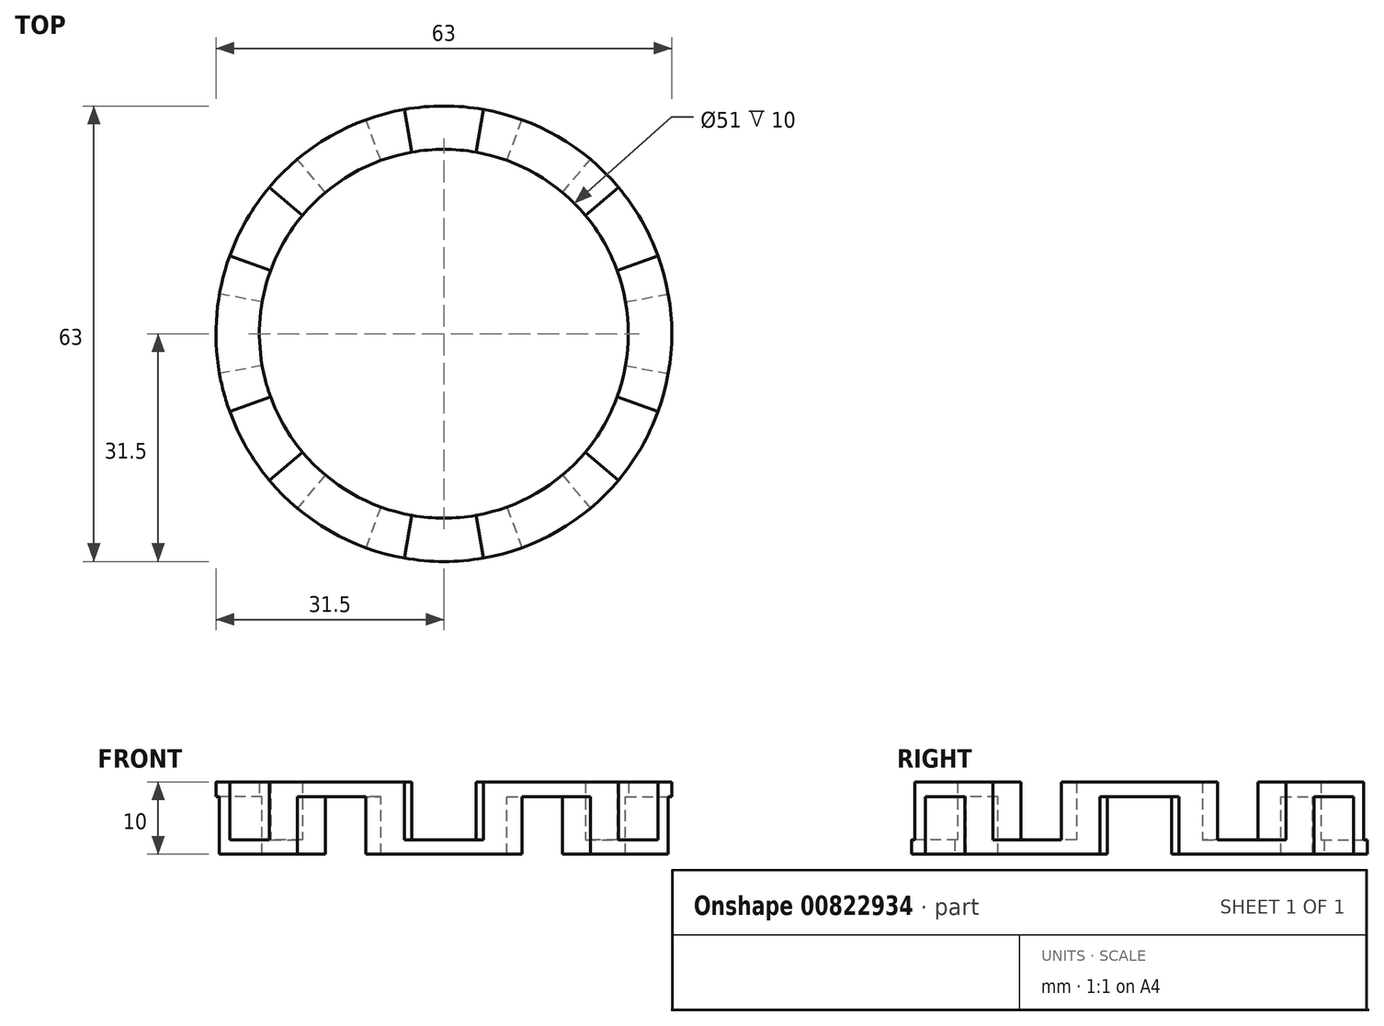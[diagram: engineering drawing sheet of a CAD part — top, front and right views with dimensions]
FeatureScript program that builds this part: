
annotation { "Feature Type Name" : "Feature", "Feature Type Description" : "" }
export const myFeature = defineFeature(function(context is Context, id is Id, definition is map)
    precondition{}
    {
        {
            var Q0;
            Q0=qCreatedBy(makeId("Top.planeOp"),FACE);
            var sketch = newSketch(context, id + "F0", { "sketchPlane" : qUnion([Q0])});
            skCircle(sketch, "E0", {"center": v(0, 0) * mm, "radius": 25.5 * mm});
            skCircle(sketch, "E1", {"center": v(0, 0) * mm, "radius": 31.5 * mm});
            skSolve(sketch);
        }
        {
            var Q0;
            Q0=makeQuery(id+"F0.imprint","IMPRINT",FACE,{"disambiguationData":[TD([[makeQuery(id+"F0.imprint","IMPRINT",EDGE,{"derivedFrom":sQuery(id+"F0.wireOp",EDGE,"E0")}),-1.0]])]});
            extrude(context, id + "F1", {"entities" : qUnion([Q0]), "endBound" : BoundingType.SYMMETRIC, "depth" : 10 * mm, "offsetDistance" : 25 * mm});
        }
        {
            var Q0;
            Q0=qCreatedBy(makeId("Top.planeOp"),FACE);
            cPlane(context, id + "F2", {"entities" : qUnion([Q0]), "cplaneType" : CPlaneType.OFFSET, "offset" : 1.25 * mm, "width" : 150 * mm, "height" : 150 * mm});
        }
        {
            var Q0;
            Q0=qCreatedBy(makeId("Top.planeOp"),FACE);
            cPlane(context, id + "F3", {"entities" : qUnion([Q0]), "cplaneType" : CPlaneType.OFFSET, "offset" : 1.25 * mm, "oppositeDirection" : true, "width" : 150 * mm, "height" : 150 * mm});
        }
        {
            var Q0;
            Q0=qCreatedBy(id+"F2.planeOp",FACE);
            var sketch = newSketch(context, id + "F4", { "sketchPlane" : qUnion([Q0])});
            skArc(sketch, "E2.0", {"start": v(23.96, 8.72) * mm, "mid": v(22.08, 12.75) * mm, "end": v(19.53, 16.4) * mm});
            skArc(sketch, "E3.0", {"start": v(29.6, 10.77) * mm, "mid": v(27.28, 15.75) * mm, "end": v(24.13, 20.25) * mm});
            skLineSegment(sketch, "E4", {"start": v(0, 0) * mm, "end": v(53.68, 0) * mm, "construction": true});
            skLineSegment(sketch, "E5", {"start": v(53.68, 0) * mm, "end": v(43, 24.82) * mm, "construction": true});
            skLineSegment(sketch, "E6", {"start": v(43, 24.82) * mm, "end": v(0, 0) * mm, "construction": true});
            skLineSegment(sketch, "E7", {"start": v(19.53, 16.4) * mm, "end": v(24.13, 20.25) * mm});
            skLineSegment(sketch, "E8.MirrorCS", {"start": v(23.96, 8.72) * mm, "end": v(29.6, 10.77) * mm});
            skLineSegment(sketch, "E9.1.0", {"start": v(-4.43, 25.11) * mm, "end": v(-5.47, 31.02) * mm});
            skArc(sketch, "E9.1.1", {"start": v(4.43, 25.11) * mm, "mid": v(0, 25.5) * mm, "end": v(-4.43, 25.11) * mm});
            skArc(sketch, "E9.1.2", {"start": v(5.47, 31.02) * mm, "mid": v(0, 31.5) * mm, "end": v(-5.47, 31.02) * mm});
            skLineSegment(sketch, "E9.1.3", {"start": v(4.43, 25.11) * mm, "end": v(5.47, 31.02) * mm});
            skLineSegment(sketch, "E9.2.0", {"start": v(-23.96, 8.72) * mm, "end": v(-29.6, 10.77) * mm});
            skArc(sketch, "E9.2.1", {"start": v(-19.53, 16.4) * mm, "mid": v(-22.08, 12.75) * mm, "end": v(-23.96, 8.72) * mm});
            skArc(sketch, "E9.2.2", {"start": v(-24.13, 20.25) * mm, "mid": v(-27.28, 15.75) * mm, "end": v(-29.6, 10.77) * mm});
            skLineSegment(sketch, "E9.2.3", {"start": v(-19.53, 16.4) * mm, "end": v(-24.13, 20.25) * mm});
            skLineSegment(sketch, "E9.3.0", {"start": v(-19.53, -16.4) * mm, "end": v(-24.13, -20.25) * mm});
            skArc(sketch, "E9.3.1", {"start": v(-23.96, -8.72) * mm, "mid": v(-22.08, -12.75) * mm, "end": v(-19.53, -16.4) * mm});
            skArc(sketch, "E9.3.2", {"start": v(-29.6, -10.77) * mm, "mid": v(-27.28, -15.75) * mm, "end": v(-24.13, -20.25) * mm});
            skLineSegment(sketch, "E9.3.3", {"start": v(-23.96, -8.72) * mm, "end": v(-29.6, -10.77) * mm});
            skLineSegment(sketch, "E9.4.0", {"start": v(4.43, -25.11) * mm, "end": v(5.47, -31.02) * mm});
            skArc(sketch, "E9.4.1", {"start": v(-4.43, -25.11) * mm, "mid": v(0, -25.5) * mm, "end": v(4.43, -25.11) * mm});
            skArc(sketch, "E9.4.2", {"start": v(-5.47, -31.02) * mm, "mid": v(0, -31.5) * mm, "end": v(5.47, -31.02) * mm});
            skLineSegment(sketch, "E9.4.3", {"start": v(-4.43, -25.11) * mm, "end": v(-5.47, -31.02) * mm});
            skLineSegment(sketch, "E9.5.0", {"start": v(23.96, -8.72) * mm, "end": v(29.6, -10.77) * mm});
            skArc(sketch, "E9.5.1", {"start": v(19.53, -16.4) * mm, "mid": v(22.08, -12.75) * mm, "end": v(23.96, -8.72) * mm});
            skArc(sketch, "E9.5.2", {"start": v(24.13, -20.25) * mm, "mid": v(27.28, -15.75) * mm, "end": v(29.6, -10.77) * mm});
            skLineSegment(sketch, "E9.5.3", {"start": v(19.53, -16.4) * mm, "end": v(24.13, -20.25) * mm});
            skSolve(sketch);
        }
        {
            var Q0;
            Q0 = qSketchRegion(id + "F4", true);
            extrude(context, id + "F5", {"entities" : qUnion([Q0]), "operationType" : NewBodyOperationType.REMOVE, "depth" : 25 * mm, "offsetDistance" : 25 * mm});
        }
        {
            var Q0;
            Q0=qCreatedBy(id+"F3.planeOp",FACE);
            var sketch = newSketch(context, id + "F6", { "sketchPlane" : qUnion([Q0])});
            skLineSegment(sketch, "E10", {"start": v(0, 0) * mm, "end": v(11.39, 0) * mm, "construction": true});
            skLineSegment(sketch, "E11", {"start": v(11.39, 0) * mm, "end": v(6.7, 11.6) * mm, "construction": true});
            skLineSegment(sketch, "E12", {"start": v(6.7, 11.6) * mm, "end": v(0, 0) * mm, "construction": true});
            skLineSegment(sketch, "E13", {"start": v(8.72, 23.96) * mm, "end": v(10.77, 29.6) * mm});
            skArc(sketch, "E14.0", {"start": v(16.4, 19.53) * mm, "mid": v(12.75, 22.08) * mm, "end": v(8.72, 23.96) * mm});
            skArc(sketch, "E15.0", {"start": v(20.25, 24.13) * mm, "mid": v(15.75, 27.28) * mm, "end": v(10.77, 29.6) * mm});
            skPoint(sketch, "E16.orphan", {"position": v(4.43, 25.11) * mm});
            skPoint(sketch, "E17.orphan", {"position": v(5.47, 31.02) * mm});
            skPoint(sketch, "E18.orphan", {"position": v(19.53, 16.4) * mm});
            skPoint(sketch, "E19.orphan", {"position": v(24.13, 20.25) * mm});
            skPoint(sketch, "E20.orphan", {"position": v(23.66, 28.2) * mm});
            skPoint(sketch, "E21.orphan", {"position": v(12.6, 34.6) * mm});
            skLineSegment(sketch, "E22.trimOffspring", {"start": v(16.4, 19.53) * mm, "end": v(20.25, 24.13) * mm});
            skArc(sketch, "E23.1.0", {"start": v(-10.77, 29.6) * mm, "mid": v(-15.75, 27.28) * mm, "end": v(-20.25, 24.13) * mm});
            skLineSegment(sketch, "E23.1.1", {"start": v(-8.72, 23.96) * mm, "end": v(-10.77, 29.6) * mm});
            skLineSegment(sketch, "E23.1.2", {"start": v(-16.4, 19.53) * mm, "end": v(-20.25, 24.13) * mm});
            skArc(sketch, "E23.1.3", {"start": v(-8.72, 23.96) * mm, "mid": v(-12.75, 22.08) * mm, "end": v(-16.4, 19.53) * mm});
            skArc(sketch, "E23.2.0", {"start": v(-31.02, 5.47) * mm, "mid": v(-31.5, 0) * mm, "end": v(-31.02, -5.47) * mm});
            skLineSegment(sketch, "E23.2.1", {"start": v(-25.11, 4.43) * mm, "end": v(-31.02, 5.47) * mm});
            skLineSegment(sketch, "E23.2.2", {"start": v(-25.11, -4.43) * mm, "end": v(-31.02, -5.47) * mm});
            skArc(sketch, "E23.2.3", {"start": v(-25.11, 4.43) * mm, "mid": v(-25.5, 0) * mm, "end": v(-25.11, -4.43) * mm});
            skArc(sketch, "E23.3.0", {"start": v(-20.25, -24.13) * mm, "mid": v(-15.75, -27.28) * mm, "end": v(-10.77, -29.6) * mm});
            skLineSegment(sketch, "E23.3.1", {"start": v(-16.4, -19.53) * mm, "end": v(-20.25, -24.13) * mm});
            skLineSegment(sketch, "E23.3.2", {"start": v(-8.72, -23.96) * mm, "end": v(-10.77, -29.6) * mm});
            skArc(sketch, "E23.3.3", {"start": v(-16.4, -19.53) * mm, "mid": v(-12.75, -22.08) * mm, "end": v(-8.72, -23.96) * mm});
            skArc(sketch, "E23.4.0", {"start": v(10.77, -29.6) * mm, "mid": v(15.75, -27.28) * mm, "end": v(20.25, -24.13) * mm});
            skLineSegment(sketch, "E23.4.1", {"start": v(8.72, -23.96) * mm, "end": v(10.77, -29.6) * mm});
            skLineSegment(sketch, "E23.4.2", {"start": v(16.4, -19.53) * mm, "end": v(20.25, -24.13) * mm});
            skArc(sketch, "E23.4.3", {"start": v(8.72, -23.96) * mm, "mid": v(12.75, -22.08) * mm, "end": v(16.4, -19.53) * mm});
            skArc(sketch, "E23.5.0", {"start": v(31.02, -5.47) * mm, "mid": v(31.5, 0) * mm, "end": v(31.02, 5.47) * mm});
            skLineSegment(sketch, "E23.5.1", {"start": v(25.11, -4.43) * mm, "end": v(31.02, -5.47) * mm});
            skLineSegment(sketch, "E23.5.2", {"start": v(25.11, 4.43) * mm, "end": v(31.02, 5.47) * mm});
            skArc(sketch, "E23.5.3", {"start": v(25.11, -4.43) * mm, "mid": v(25.5, 0) * mm, "end": v(25.11, 4.43) * mm});
            skSolve(sketch);
        }
        {
            var Q0;
            Q0 = qSketchRegion(id + "F6", true);
            extrude(context, id + "F7", {"entities" : qUnion([Q0]), "operationType" : NewBodyOperationType.REMOVE, "oppositeDirection" : true, "depth" : 25 * mm, "offsetDistance" : 25 * mm});
        }
        {
            var Q0;
            Q0=makeQuery(id+"F5.boolean.opBoolean","COPY",FACE,{"derivedFrom":makeQuery(id+"F5.opExtrude","CAP_FACE",FACE,{"disambiguationData":[OSD([sQuery(id+"F4.wireOp",EDGE,"E9.3.0"),sQuery(id+"F4.wireOp",EDGE,"E9.3.1"),sQuery(id+"F4.wireOp",EDGE,"E9.3.2"),sQuery(id+"F4.wireOp",EDGE,"E9.3.3")])],"isStart":true})});
            var Q1;
            Q1=makeQuery(id+"F5.boolean.opBoolean","COPY",FACE,{"derivedFrom":makeQuery(id+"F5.opExtrude","CAP_FACE",FACE,{"disambiguationData":[OSD([sQuery(id+"F4.wireOp",EDGE,"E9.2.0"),sQuery(id+"F4.wireOp",EDGE,"E9.2.1"),sQuery(id+"F4.wireOp",EDGE,"E9.2.2"),sQuery(id+"F4.wireOp",EDGE,"E9.2.3")])],"isStart":true})});
            var Q2;
            Q2=makeQuery(id+"F5.boolean.opBoolean","COPY",FACE,{"derivedFrom":makeQuery(id+"F5.opExtrude","CAP_FACE",FACE,{"disambiguationData":[OSD([sQuery(id+"F4.wireOp",EDGE,"E9.1.0"),sQuery(id+"F4.wireOp",EDGE,"E9.1.1"),sQuery(id+"F4.wireOp",EDGE,"E9.1.2"),sQuery(id+"F4.wireOp",EDGE,"E9.1.3")])],"isStart":true})});
            var Q3;
            Q3=makeQuery(id+"F5.boolean.opBoolean","COPY",FACE,{"derivedFrom":makeQuery(id+"F5.opExtrude","CAP_FACE",FACE,{"disambiguationData":[OSD([sQuery(id+"F4.wireOp",EDGE,"E2.0"),sQuery(id+"F4.wireOp",EDGE,"E3.0"),sQuery(id+"F4.wireOp",EDGE,"E7"),sQuery(id+"F4.wireOp",EDGE,"E8.MirrorCS")])],"isStart":true})});
            var Q4;
            Q4=makeQuery(id+"F5.boolean.opBoolean","COPY",FACE,{"derivedFrom":makeQuery(id+"F5.opExtrude","CAP_FACE",FACE,{"disambiguationData":[OSD([sQuery(id+"F4.wireOp",EDGE,"E9.5.0"),sQuery(id+"F4.wireOp",EDGE,"E9.5.1"),sQuery(id+"F4.wireOp",EDGE,"E9.5.2"),sQuery(id+"F4.wireOp",EDGE,"E9.5.3")])],"isStart":true})});
            var Q5;
            Q5=makeQuery(id+"F5.boolean.opBoolean","COPY",FACE,{"derivedFrom":makeQuery(id+"F5.opExtrude","CAP_FACE",FACE,{"disambiguationData":[OSD([sQuery(id+"F4.wireOp",EDGE,"E9.4.0"),sQuery(id+"F4.wireOp",EDGE,"E9.4.1"),sQuery(id+"F4.wireOp",EDGE,"E9.4.2"),sQuery(id+"F4.wireOp",EDGE,"E9.4.3")])],"isStart":true})});
            extrude(context, id + "F8", {"entities" : qUnion([Q0, Q1, Q2, Q3, Q4, Q5]), "operationType" : NewBodyOperationType.REMOVE, "oppositeDirection" : true, "depth" : 4.25 * mm, "offsetDistance" : 25 * mm});
        }
        {
            var Q0;
            Q0=makeQuery(id+"F7.boolean.opBoolean","COPY",FACE,{"derivedFrom":makeQuery(id+"F7.opExtrude","CAP_FACE",FACE,{"disambiguationData":[OSD([sQuery(id+"F6.wireOp",EDGE,"E23.3.0"),sQuery(id+"F6.wireOp",EDGE,"E23.3.1"),sQuery(id+"F6.wireOp",EDGE,"E23.3.2"),sQuery(id+"F6.wireOp",EDGE,"E23.3.3")])],"isStart":true})});
            var Q1;
            Q1=makeQuery(id+"F7.boolean.opBoolean","COPY",FACE,{"derivedFrom":makeQuery(id+"F7.opExtrude","CAP_FACE",FACE,{"disambiguationData":[OSD([sQuery(id+"F6.wireOp",EDGE,"E23.4.0"),sQuery(id+"F6.wireOp",EDGE,"E23.4.1"),sQuery(id+"F6.wireOp",EDGE,"E23.4.2"),sQuery(id+"F6.wireOp",EDGE,"E23.4.3")])],"isStart":true})});
            var Q2;
            Q2=makeQuery(id+"F7.boolean.opBoolean","COPY",FACE,{"derivedFrom":makeQuery(id+"F7.opExtrude","CAP_FACE",FACE,{"disambiguationData":[OSD([sQuery(id+"F6.wireOp",EDGE,"E23.5.0"),sQuery(id+"F6.wireOp",EDGE,"E23.5.1"),sQuery(id+"F6.wireOp",EDGE,"E23.5.2"),sQuery(id+"F6.wireOp",EDGE,"E23.5.3")])],"isStart":true})});
            var Q3;
            Q3=makeQuery(id+"F7.boolean.opBoolean","COPY",FACE,{"derivedFrom":makeQuery(id+"F7.opExtrude","CAP_FACE",FACE,{"disambiguationData":[OSD([sQuery(id+"F6.wireOp",EDGE,"E13"),sQuery(id+"F6.wireOp",EDGE,"E14.0"),sQuery(id+"F6.wireOp",EDGE,"E15.0"),sQuery(id+"F6.wireOp",EDGE,"E22.trimOffspring")])],"isStart":true})});
            var Q4;
            Q4=makeQuery(id+"F7.boolean.opBoolean","COPY",FACE,{"derivedFrom":makeQuery(id+"F7.opExtrude","CAP_FACE",FACE,{"disambiguationData":[OSD([sQuery(id+"F6.wireOp",EDGE,"E23.1.0"),sQuery(id+"F6.wireOp",EDGE,"E23.1.1"),sQuery(id+"F6.wireOp",EDGE,"E23.1.2"),sQuery(id+"F6.wireOp",EDGE,"E23.1.3")])],"isStart":true})});
            var Q5;
            Q5=makeQuery(id+"F7.boolean.opBoolean","COPY",FACE,{"derivedFrom":makeQuery(id+"F7.opExtrude","CAP_FACE",FACE,{"disambiguationData":[OSD([sQuery(id+"F6.wireOp",EDGE,"E23.2.0"),sQuery(id+"F6.wireOp",EDGE,"E23.2.1"),sQuery(id+"F6.wireOp",EDGE,"E23.2.2"),sQuery(id+"F6.wireOp",EDGE,"E23.2.3")])],"isStart":true})});
            extrude(context, id + "F9", {"entities" : qUnion([Q0, Q1, Q2, Q3, Q4, Q5]), "operationType" : NewBodyOperationType.REMOVE, "oppositeDirection" : true, "depth" : 4.25 * mm, "offsetDistance" : 25 * mm});
        }
    });
